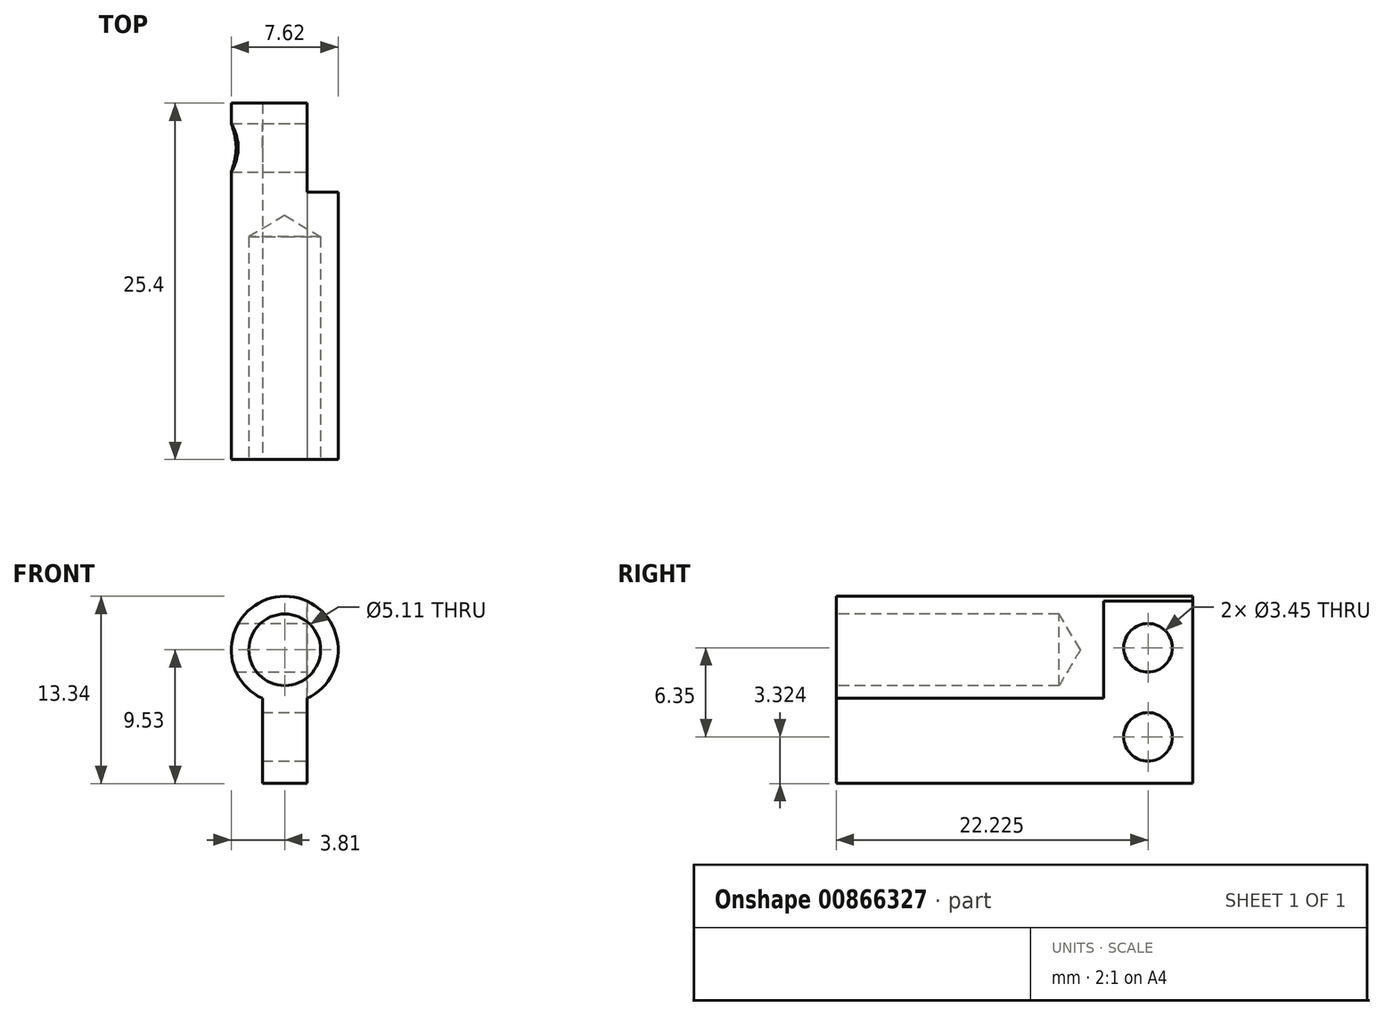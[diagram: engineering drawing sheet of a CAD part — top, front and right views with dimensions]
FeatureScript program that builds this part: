
annotation { "Feature Type Name" : "Feature", "Feature Type Description" : "" }
export const myFeature = defineFeature(function(context is Context, id is Id, definition is map)
    precondition{}
    {
        {
            var Q0;
            Q0=qCreatedBy(makeId("Front.planeOp"),FACE);
            var sketch = newSketch(context, id + "F0", { "sketchPlane" : qUnion([Q0])});
            skCircle(sketch, "E0", {"center": v(0, 0) * mm, "radius": 3.81 * mm});
            skLineSegment(sketch, "E1.bottom", {"start": v(-1.59, 0) * mm, "end": v(1.59, 0) * mm});
            skLineSegment(sketch, "E1.top", {"start": v(-1.59, -9.53) * mm, "end": v(1.59, -9.53) * mm});
            skLineSegment(sketch, "E1.left", {"start": v(-1.59, 0) * mm, "end": v(-1.59, -9.53) * mm});
            skLineSegment(sketch, "E1.right", {"start": v(1.59, 0) * mm, "end": v(1.59, -9.53) * mm});
            skPoint(sketch, "E1.middle", {"position": v(0, -4.76) * mm});
            skSolve(sketch);
        }
        {
            var Q0;
            Q0 = qSketchRegion(id + "F0", true);
            extrude(context, id + "F1", {"entities" : qUnion([Q0]), "oppositeDirection" : true, "depth" : 25.4 * mm, "offsetDistance" : 25.4 * mm});
        }
        {
            var Q0;
            Q0=sQuery(id+"F0.wireOp",VERTEX,"E0.center");
            var Q1;
            Q1=makeQuery(id+"F1.opExtrude","SWEPT_BODY",BODY,{"disambiguationData":[OSD([sQuery(id+"F0.wireOp",EDGE,"E0"),sQuery(id+"F0.wireOp",EDGE,"E1.top"),sQuery(id+"F0.wireOp",EDGE,"E1.left"),sQuery(id+"F0.wireOp",EDGE,"E1.right")])]});
            hole(context, id + "F2", {"style" : HoleStyle.SIMPLE, "endStyle" : HoleEndStyle.BLIND, "standardTappedOrClearance" : lookupTablePath({ "standard" : "ANSI", "engagement" : "75%", "pitch" : "20 tpi", "size" : "1/4", "type" : "Tapped" }), "standardBlindInLast" : lookupTablePath({ "standard" : "ANSI", "engagement" : "75%", "pitch" : "20 tpi", "size" : "1/4", "type" : "Tapped" }), "holeDiameter" : 5.1 * mm, "majorDiameter" : 6.35 * mm, "showTappedDepth" : true, "holeDepth" : 15.88 * mm, "isTappedThrough" : true, "tappedDepth" : 12.06 * mm, "tapClearance" : 3, "locations" : qUnion([Q0]), "scope" : qUnion([Q1])});
        }
        {
            var Q0;
            Q0=makeQuery(id+"F1.opExtrude","SWEPT_FACE",FACE,{"disambiguationData":[OSD([sQuery(id+"F0.wireOp",EDGE,"E1.right")])]});
            var sketch = newSketch(context, id + "F3", { "sketchPlane" : qUnion([Q0])});
            skLineSegment(sketch, "E2.bottom", {"start": v(25.4, -3.46) * mm, "end": v(19.05, -3.46) * mm});
            skLineSegment(sketch, "E2.top", {"start": v(25.4, 3.81) * mm, "end": v(19.05, 3.8) * mm});
            skLineSegment(sketch, "E2.left", {"start": v(25.4, -3.46) * mm, "end": v(25.4, 3.81) * mm});
            skLineSegment(sketch, "E2.right", {"start": v(19.05, -3.46) * mm, "end": v(19.05, 3.8) * mm});
            skSolve(sketch);
        }
        {
            var Q0;
            Q0 = qSketchRegion(id + "F3", true);
            extrude(context, id + "F4", {"entities" : qUnion([Q0]), "operationType" : NewBodyOperationType.REMOVE, "endBound" : BoundingType.THROUGH_ALL, "depth" : 25.4 * mm, "offsetDistance" : 25.4 * mm});
        }
        {
            var Q0;
            Q0=makeQuery(id+"F4.boolean.opBoolean","MERGE",FACE,{"derivedFrom":[makeQuery(id+"F1.opExtrude","SWEPT_FACE",FACE,{"disambiguationData":[OSD([sQuery(id+"F0.wireOp",EDGE,"E1.right")])]})],"fromTools":[makeQuery(id+"F4.opExtrude","CAP_FACE",FACE,{"disambiguationData":[OSD([sQuery(id+"F3.wireOp",EDGE,"E2.bottom"),sQuery(id+"F3.wireOp",EDGE,"E2.top"),sQuery(id+"F3.wireOp",EDGE,"E2.left"),sQuery(id+"F3.wireOp",EDGE,"E2.right")])],"isStart":true})]});
            var sketch = newSketch(context, id + "F5", { "sketchPlane" : qUnion([Q0])});
            skLineSegment(sketch, "E3", {"start": v(22.23, 3.46) * mm, "end": v(22.23, 0.14) * mm});
            skLineSegment(sketch, "E4", {"start": v(22.23, 0.14) * mm, "end": v(22.23, -6.2) * mm});
            skLineSegment(sketch, "E5", {"start": v(22.23, -6.2) * mm, "end": v(22.23, -9.53) * mm});
            skSolve(sketch);
        }
        {
            var Q0;
            Q0=sQuery(id+"F5.wireOp",VERTEX,"E3.end");
            var Q1;
            Q1=sQuery(id+"F5.wireOp",VERTEX,"E4.end");
            var Q2;
            Q2=makeQuery(id+"F1.opExtrude","SWEPT_BODY",BODY,{"disambiguationData":[OSD([sQuery(id+"F0.wireOp",EDGE,"E0"),sQuery(id+"F0.wireOp",EDGE,"E1.top"),sQuery(id+"F0.wireOp",EDGE,"E1.left"),sQuery(id+"F0.wireOp",EDGE,"E1.right")])]});
            hole(context, id + "F6", {"style" : HoleStyle.SIMPLE, "endStyle" : HoleEndStyle.THROUGH, "standardTappedOrClearance" : lookupTablePath({ "standard" : "ANSI", "engagement" : "75%", "pitch" : "32 tpi", "size" : "#8", "type" : "Tapped" }), "standardBlindInLast" : lookupTablePath({ "standard" : "ANSI", "engagement" : "75%", "pitch" : "32 tpi", "size" : "#8", "type" : "Tapped" }), "holeDiameter" : 3.45 * mm, "majorDiameter" : 4.17 * mm, "showTappedDepth" : true, "isTappedThrough" : true, "tappedDepth" : 12.06 * mm, "tapClearance" : 3, "locations" : qUnion([Q0, Q1]), "scope" : qUnion([Q2])});
        }
    });
